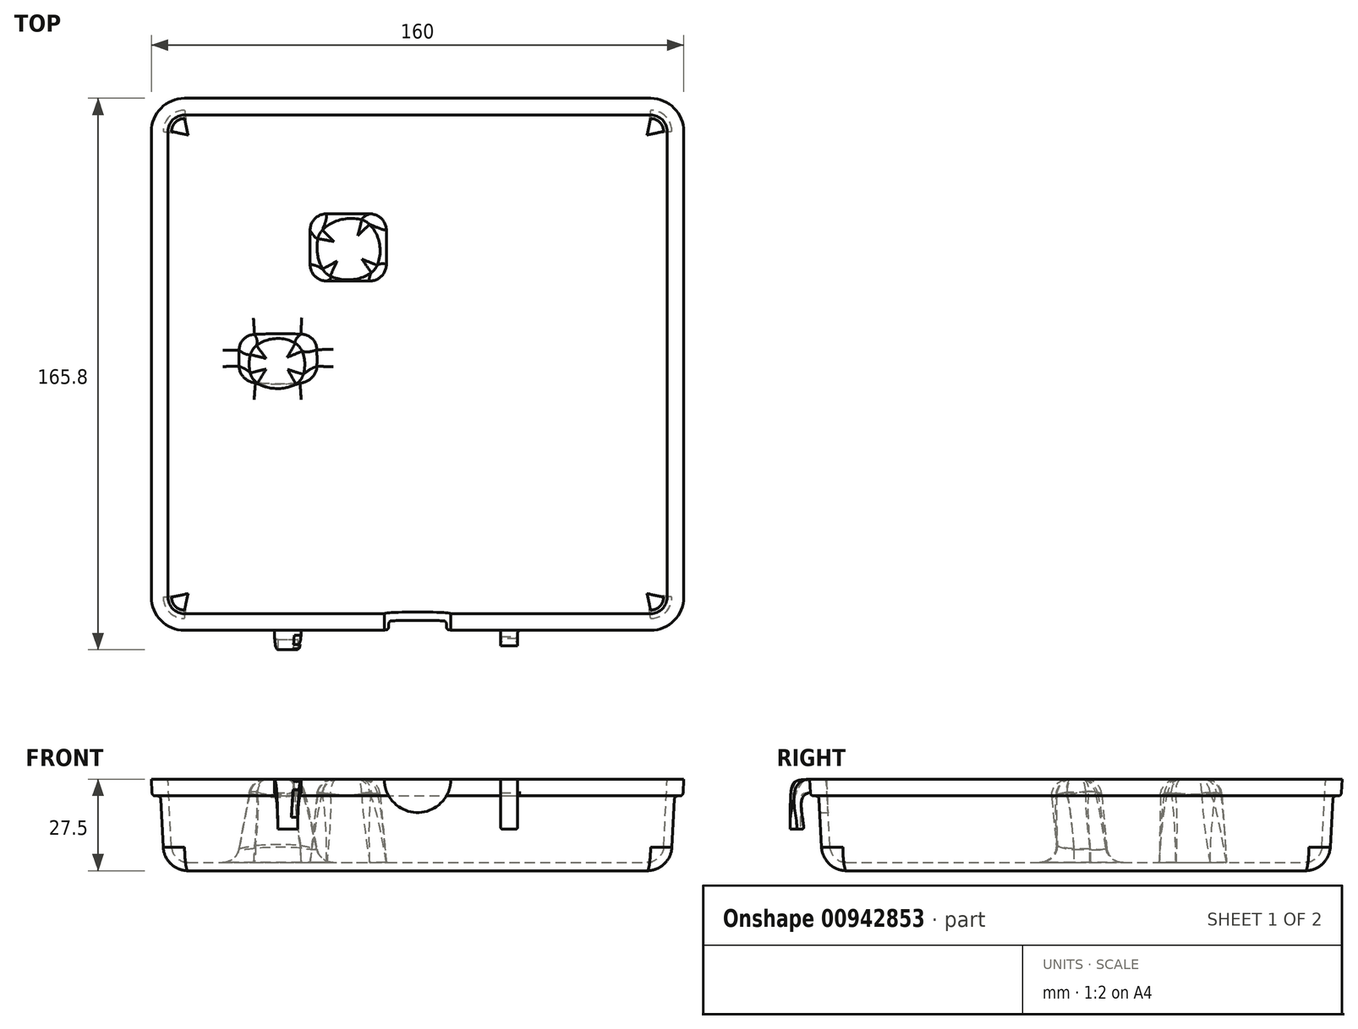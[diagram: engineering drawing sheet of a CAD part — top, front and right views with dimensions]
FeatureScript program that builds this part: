
annotation { "Feature Type Name" : "Feature", "Feature Type Description" : "" }
export const myFeature = defineFeature(function(context is Context, id is Id, definition is map)
    precondition{}
    {
        {
            var Q0;
            Q0=qCreatedBy(makeId("Top.planeOp"),FACE);
            var sketch = newSketch(context, id + "F0", { "sketchPlane" : qUnion([Q0])});
            skLineSegment(sketch, "E0.bottom", {"start": v(5, 0) * mm, "end": v(145, 0) * mm});
            skLineSegment(sketch, "E0.top", {"start": v(5, 150) * mm, "end": v(145, 150) * mm});
            skLineSegment(sketch, "E0.left", {"start": v(0, 5) * mm, "end": v(0, 145) * mm});
            skLineSegment(sketch, "E0.right", {"start": v(150, 5) * mm, "end": v(150, 145) * mm});
            skLineSegment(sketch, "E1.0", {"start": v(-5, 5) * mm, "end": v(-5, 145) * mm});
            skLineSegment(sketch, "E1.1", {"start": v(5, -5) * mm, "end": v(145, -5) * mm});
            skLineSegment(sketch, "E1.2", {"start": v(155, 5) * mm, "end": v(155, 145) * mm});
            skLineSegment(sketch, "E1.3", {"start": v(5, 155) * mm, "end": v(145, 155) * mm});
            skPoint(sketch, "E2.visualSharp", {"position": v(0, 150) * mm});
            skArc(sketch, "E2.filletArc", {"start": v(5, 150) * mm, "mid": v(1.46, 148.54) * mm, "end": v(0, 145) * mm});
            skPoint(sketch, "E3.visualSharp", {"position": v(150, 150) * mm});
            skArc(sketch, "E3.filletArc", {"start": v(150, 145) * mm, "mid": v(148.54, 148.54) * mm, "end": v(145, 150) * mm});
            skPoint(sketch, "E4.visualSharp", {"position": v(150, 0) * mm});
            skArc(sketch, "E4.filletArc", {"start": v(145, 0) * mm, "mid": v(148.54, 1.46) * mm, "end": v(150, 5) * mm});
            skPoint(sketch, "E5.visualSharp", {"position": v(0, 0) * mm});
            skArc(sketch, "E5.filletArc", {"start": v(0, 5) * mm, "mid": v(1.46, 1.46) * mm, "end": v(5, 0) * mm});
            skPoint(sketch, "E6.visualSharp", {"position": v(-5, 155) * mm});
            skArc(sketch, "E6.filletArc", {"start": v(5, 155) * mm, "mid": v(-2.07, 152.07) * mm, "end": v(-5, 145) * mm});
            skPoint(sketch, "E7.visualSharp", {"position": v(155, 155) * mm});
            skArc(sketch, "E7.filletArc", {"start": v(155, 145) * mm, "mid": v(152.07, 152.07) * mm, "end": v(145, 155) * mm});
            skPoint(sketch, "E8.visualSharp", {"position": v(155, -5) * mm});
            skArc(sketch, "E8.filletArc", {"start": v(145, -5) * mm, "mid": v(152.07, -2.07) * mm, "end": v(155, 5) * mm});
            skPoint(sketch, "E9.visualSharp", {"position": v(-5, -5) * mm});
            skArc(sketch, "E9.filletArc", {"start": v(-5, 5) * mm, "mid": v(-2.07, -2.07) * mm, "end": v(5, -5) * mm});
            skSolve(sketch);
        }
        {
            var Q0;
            Q0=makeQuery(id+"F0.imprint","IMPRINT",FACE,{"disambiguationData":[TD([[makeQuery(id+"F0.imprint","IMPRINT",EDGE,{"derivedFrom":sQuery(id+"F0.wireOp",EDGE,"E0.bottom")}),1.0]])]});
            extrude(context, id + "F1", {"entities" : qUnion([Q0]), "oppositeDirection" : true, "depth" : 25 * mm, "hasDraft" : true, "draftAngle" : 3 * degree, "draftPullDirection" : true});
        }
        {
            var Q0;
            Q0=makeQuery(id+"F1.opExtrude","SWEPT_EDGE",EDGE,{"disambiguationData":[OSD([sQuery(id+"F0.wireOp",EDGE,"E0.bottom"),sQuery(id+"F0.wireOp",EDGE,"E0.left")])]});
            var Q1;
            Q1=makeQuery(id+"F1.opExtrude","SWEPT_EDGE",EDGE,{"disambiguationData":[OSD([sQuery(id+"F0.wireOp",EDGE,"E0.bottom"),sQuery(id+"F0.wireOp",EDGE,"E0.right")])]});
            var Q2;
            Q2=makeQuery(id+"F1.opExtrude","SWEPT_EDGE",EDGE,{"disambiguationData":[OSD([sQuery(id+"F0.wireOp",EDGE,"E0.top"),sQuery(id+"F0.wireOp",EDGE,"E0.left")])]});
            var Q3;
            Q3=makeQuery(id+"F1.opExtrude","SWEPT_EDGE",EDGE,{"disambiguationData":[OSD([sQuery(id+"F0.wireOp",EDGE,"E0.top"),sQuery(id+"F0.wireOp",EDGE,"E0.right")])]});
            var Q4;
            Q4=makeQuery(id+"F1.opExtrude","CAP_FACE",FACE,{"disambiguationData":[OSD([sQuery(id+"F0.wireOp",EDGE,"E0.bottom"),sQuery(id+"F0.wireOp",EDGE,"E0.top"),sQuery(id+"F0.wireOp",EDGE,"E0.left"),sQuery(id+"F0.wireOp",EDGE,"E0.right")])],"isStart":false});
            fillet(context, id + "F2", {"entities" : qUnion([Q0, Q1, Q2, Q3, Q4]), "radius" : 5 * mm, "tangentPropagation" : true, "allowEdgeOverflow" : false});
        }
        {
            var Q0;
            Q0=makeQuery(id+"F1.opExtrude","CAP_FACE",FACE,{"disambiguationData":[OSD([sQuery(id+"F0.wireOp",EDGE,"E0.bottom"),sQuery(id+"F0.wireOp",EDGE,"E0.top"),sQuery(id+"F0.wireOp",EDGE,"E0.left"),sQuery(id+"F0.wireOp",EDGE,"E0.right")])],"isStart":true});
            shell(context, id + "F3", {"entities" : qUnion([Q0]), "thickness" : 2.5 * mm, "oppositeDirection" : true});
        }
        {
            var Q0;
            Q0=makeQuery(id+"F0.imprint","IMPRINT",FACE,{"disambiguationData":[TD([[makeQuery(id+"F0.imprint","IMPRINT",EDGE,{"derivedFrom":sQuery(id+"F0.wireOp",EDGE,"E0.bottom")}),-1.0]])]});
            extrude(context, id + "F4", {"entities" : qUnion([Q0]), "operationType" : NewBodyOperationType.ADD, "oppositeDirection" : true, "depth" : 5 * mm, "hasDraft" : true, "draftAngle" : 3 * degree, "draftPullDirection" : true});
        }
        {
            var Q0;
            {var subQ0=sQuery(id+"F0.wireOp",EDGE,"E0.bottom");Q0=makeQuery(id+"F4.boolean.opBoolean","INTERSECT",EDGE,{"derivedFrom":[makeQuery(id+"F1.opExtrude","SWEPT_FACE",FACE,{"disambiguationData":[OSD([subQ0])]}),makeQuery(id+"F4.opExtrude","CAP_FACE",FACE,{"disambiguationData":[OSD([subQ0,sQuery(id+"F0.wireOp",EDGE,"E0.top"),sQuery(id+"F0.wireOp",EDGE,"E0.left"),sQuery(id+"F0.wireOp",EDGE,"E0.right"),sQuery(id+"F0.wireOp",EDGE,"E1.0"),sQuery(id+"F0.wireOp",EDGE,"E1.1"),sQuery(id+"F0.wireOp",EDGE,"E1.2"),sQuery(id+"F0.wireOp",EDGE,"E1.3"),sQuery(id+"F0.wireOp",EDGE,"E2.filletArc"),sQuery(id+"F0.wireOp",EDGE,"E3.filletArc"),sQuery(id+"F0.wireOp",EDGE,"E4.filletArc"),sQuery(id+"F0.wireOp",EDGE,"E5.filletArc"),sQuery(id+"F0.wireOp",EDGE,"E6.filletArc"),sQuery(id+"F0.wireOp",EDGE,"E7.filletArc"),sQuery(id+"F0.wireOp",EDGE,"E8.filletArc"),sQuery(id+"F0.wireOp",EDGE,"E9.filletArc")])],"isStart":false})]});}
            var Q1;
            Q1=makeQuery(id+"F4.opExtrude","CAP_EDGE",EDGE,{"disambiguationData":[OSD([sQuery(id+"F0.wireOp",EDGE,"E1.1")])],"isStart":false});
            fillet(context, id + "F5", {"entities" : qUnion([Q0, Q1]), "radius" : 1 * mm, "tangentPropagation" : true, "allowEdgeOverflow" : false});
        }
        {
            var Q0;
            Q0=qCreatedBy(makeId("Front.planeOp"),FACE);
            var sketch = newSketch(context, id + "F6", { "sketchPlane" : qUnion([Q0])});
            skCircle(sketch, "E10", {"center": v(75, 0) * mm, "radius": 10 * mm});
            skSolve(sketch);
        }
        {
            var Q0;
            Q0=qSketchRegion(id+"F6",true);
            extrude(context, id + "F7", {"entities" : qUnion([Q0]), "operationType" : NewBodyOperationType.REMOVE, "endBound" : BoundingType.SYMMETRIC, "depth" : 25 * mm});
        }
        {
            var Q0;
            Q0=qCreatedBy(makeId("Top.planeOp"),FACE);
            cPlane(context, id + "F8", {"entities" : qUnion([Q0]), "cplaneType" : CPlaneType.OFFSET, "offset" : 15 * mm, "oppositeDirection" : true, "width" : 150 * mm, "height" : 150 * mm});
        }
        {
            var Q0;
            {var subQ0=sQuery(id+"F0.wireOp",EDGE,"E1.1");var subQ1=sQuery(id+"F0.wireOp",EDGE,"E8.filletArc");Q0=makeQuery(id+"F7.boolean.opBoolean","SPLIT",FACE,{"disambiguationData":[TD([makeQuery(id+"F4.opExtrude","SWEPT_FACE",FACE,{"disambiguationData":[OSD([subQ1])]})])],"derivedFrom":makeQuery(id+"F4.opExtrude","SWEPT_FACE",FACE,{"disambiguationData":[OSD([subQ0])]})});}
            var sketch = newSketch(context, id + "F9", { "sketchPlane" : qUnion([Q0])});
            skLineSegment(sketch, "E11.bottom", {"start": v(100, 0.26) * mm, "end": v(105, 0.26) * mm});
            skLineSegment(sketch, "E11.top", {"start": v(100, -3.8) * mm, "end": v(105, -3.8) * mm});
            skLineSegment(sketch, "E11.left", {"start": v(100, 0.26) * mm, "end": v(100, -3.8) * mm});
            skLineSegment(sketch, "E11.right", {"start": v(105, 0.26) * mm, "end": v(105, -3.8) * mm});
            skSolve(sketch);
        }
        {
            var Q0;
            Q0=qCreatedBy(id+"F8.planeOp",FACE);
            var sketch = newSketch(context, id + "F10", { "sketchPlane" : qUnion([Q0])});
            skLineSegment(sketch, "E12.bottom", {"start": v(100, -6.79) * mm, "end": v(105, -6.79) * mm});
            skLineSegment(sketch, "E12.top", {"start": v(100, -8.79) * mm, "end": v(105, -8.79) * mm});
            skLineSegment(sketch, "E12.left", {"start": v(100, -6.79) * mm, "end": v(100, -8.79) * mm});
            skLineSegment(sketch, "E12.right", {"start": v(105, -6.79) * mm, "end": v(105, -8.79) * mm});
            skSolve(sketch);
        }
        {
            var Q1;
            Q1=makeQuery(id+"F9.imprint","IMPRINT",FACE,{"disambiguationData":[TD([[makeQuery(id+"F9.imprint","IMPRINT",EDGE,{"derivedFrom":sQuery(id+"F9.wireOp",EDGE,"E11.bottom")}),-1.0]])]});
            var Q2;
            Q2=makeQuery(id+"F10.imprint","IMPRINT",FACE,{"disambiguationData":[TD([[makeQuery(id+"F10.imprint","IMPRINT",EDGE,{"derivedFrom":sQuery(id+"F10.wireOp",EDGE,"E12.bottom")}),-1.0]])]});
            loft(context, id + "F11", {"operationType" : NewBodyOperationType.ADD, "startCondition" : LoftEndDerivativeType.NORMAL_TO_PROFILE, "startMagnitude" : 4, "endCondition" : LoftEndDerivativeType.NORMAL_TO_PROFILE, "endMagnitude" : 1, "sheetProfilesArray" : [{ "sheetProfileEntities" : qUnion([Q1]) }, { "sheetProfileEntities" : qUnion([Q2]) }]});
        }
        {
            var Q0;
            Q0=makeQuery(id+"F11.opLoft","MID_CAP_EDGE",EDGE,{"disambiguationData":[OSD([sQuery(id+"F0.wireOp",EDGE,"E1.1"),sQuery(id+"F9.wireOp",EDGE,"E11.bottom"),sQuery(id+"F9.wireOp",EDGE,"E11.top"),sQuery(id+"F9.wireOp",EDGE,"E11.right")])],"capPos":0.0});
            fillet(context, id + "F12", {"entities" : qUnion([Q0]), "radius" : 1 * mm, "tangentPropagation" : true, "allowEdgeOverflow" : false});
        }
        {
            var Q0;
            Q0=makeQuery(id+"F11.opLoft","CAP_FACE",FACE,{"disambiguationData":[OSD([makeQuery(id+"F10.imprint","IMPRINT",FACE,{"disambiguationData":[TD([[makeQuery(id+"F10.imprint","IMPRINT",EDGE,{"derivedFrom":sQuery(id+"F10.wireOp",EDGE,"E12.bottom")}),-1.0]])]})])],"isStart":true});
            fillet(context, id + "F13", {"entities" : qUnion([Q0]), "radius" : .5 * mm, "tangentPropagation" : true, "allowEdgeOverflow" : false});
        }
        {
            var Q0;
            Q0=makeQuery(id+"F3.opShell","OFFSET_FACE",FACE,{"disambiguationData":[OSD([sQuery(id+"F0.wireOp",EDGE,"E0.bottom"),sQuery(id+"F0.wireOp",EDGE,"E0.top"),sQuery(id+"F0.wireOp",EDGE,"E0.left"),sQuery(id+"F0.wireOp",EDGE,"E0.right"),sQuery(id+"F0.wireOp",EDGE,"E2.filletArc"),sQuery(id+"F0.wireOp",EDGE,"E3.filletArc"),sQuery(id+"F0.wireOp",EDGE,"E4.filletArc"),sQuery(id+"F0.wireOp",EDGE,"E5.filletArc")])]});
            var sketch = newSketch(context, id + "F14", { "sketchPlane" : qUnion([Q0])});
            skLineSegment(sketch, "E13.bottom", {"start": v(42.7, 100.07) * mm, "end": v(65.63, 100.07) * mm});
            skLineSegment(sketch, "E13.top", {"start": v(42.7, 120.25) * mm, "end": v(65.63, 120.25) * mm});
            skLineSegment(sketch, "E13.left", {"start": v(42.7, 100.07) * mm, "end": v(42.7, 120.25) * mm});
            skLineSegment(sketch, "E13.right", {"start": v(65.63, 100.07) * mm, "end": v(65.63, 120.25) * mm});
            skSolve(sketch);
        }
        {
            var Q0;
            Q0=qCreatedBy(makeId("Top.planeOp"),FACE);
            var sketch = newSketch(context, id + "F15", { "sketchPlane" : qUnion([Q0])});
            skArc(sketch, "E14", {"start": v(48.26, 102.79) * mm, "mid": v(55.2, 100.54) * mm, "end": v(61.55, 104.16) * mm});
            skArc(sketch, "E15", {"start": v(58.35, 117.61) * mm, "mid": v(51.16, 118.02) * mm, "end": v(45.95, 113.06) * mm});
            skArc(sketch, "E16", {"start": v(45.95, 113.06) * mm, "mid": v(45.46, 107.55) * mm, "end": v(48.26, 102.79) * mm});
            skArc(sketch, "E17", {"start": v(61.55, 104.16) * mm, "mid": v(63.08, 111.63) * mm, "end": v(58.35, 117.61) * mm});
            skSolve(sketch);
        }
        {
            var Q1;
            Q1=makeQuery(id+"F14.imprint","IMPRINT",FACE,{"disambiguationData":[TD([[makeQuery(id+"F14.imprint","IMPRINT",EDGE,{"derivedFrom":sQuery(id+"F14.wireOp",EDGE,"E13.bottom")}),1.0]])]});
            var Q2;
            Q2=makeQuery(id+"F15.imprint","IMPRINT",FACE,{"disambiguationData":[TD([[makeQuery(id+"F15.imprint","IMPRINT",EDGE,{"derivedFrom":sQuery(id+"F15.wireOp",EDGE,"E14")}),1.0]])]});
            var Q3;
            Q3=sQuery(id+"F14.wireOp",VERTEX,"E13.right.start");
            var Q4;
            Q4=sQuery(id+"F15.wireOp",VERTEX,"E16.end");
            loft(context, id + "F16", {"operationType" : NewBodyOperationType.ADD, "sheetProfilesArray" : [{ "sheetProfileEntities" : qUnion([Q1]) }, { "sheetProfileEntities" : qUnion([Q2]) }], "connections" : [{ "connectionEntities" : qUnion([Q3, Q4]), "connectionEdgeQueries" : qUnion([]), "connectionEdgeParameters" : [] }]});
        }
        {
            var Q0;
            Q0=makeQuery(id+"F16.opLoft","SWEPT_EDGE",EDGE,{"disambiguationData":[OSD([sQuery(id+"F14.wireOp",EDGE,"E13.bottom"),sQuery(id+"F14.wireOp",EDGE,"E13.left"),sQuery(id+"F15.wireOp",EDGE,"E14"),sQuery(id+"F15.wireOp",EDGE,"E16")])]});
            var Q1;
            Q1=makeQuery(id+"F16.opLoft","SWEPT_EDGE",EDGE,{"disambiguationData":[OSD([sQuery(id+"F14.wireOp",EDGE,"E13.bottom"),sQuery(id+"F14.wireOp",EDGE,"E13.right"),sQuery(id+"F15.wireOp",EDGE,"E14"),sQuery(id+"F15.wireOp",EDGE,"E17")])]});
            var Q2;
            Q2=makeQuery(id+"F16.opLoft","SWEPT_EDGE",EDGE,{"disambiguationData":[OSD([sQuery(id+"F14.wireOp",EDGE,"E13.top"),sQuery(id+"F14.wireOp",EDGE,"E13.right"),sQuery(id+"F15.wireOp",EDGE,"E15"),sQuery(id+"F15.wireOp",EDGE,"E17")])]});
            var Q3;
            Q3=makeQuery(id+"F16.opLoft","SWEPT_EDGE",EDGE,{"disambiguationData":[OSD([sQuery(id+"F14.wireOp",EDGE,"E13.top"),sQuery(id+"F14.wireOp",EDGE,"E13.left"),sQuery(id+"F15.wireOp",EDGE,"E15"),sQuery(id+"F15.wireOp",EDGE,"E16")])]});
            fillet(context, id + "F17", {"entities" : qUnion([Q0, Q1, Q2, Q3]), "radius" : 5 * mm, "tangentPropagation" : true, "allowEdgeOverflow" : false});
        }
        {
            var Q0;
            Q0=makeQuery(id+"F16.opLoft","MID_CAP_EDGE",EDGE,{"disambiguationData":[OSD([sQuery(id+"F14.wireOp",EDGE,"E13.bottom"),sQuery(id+"F14.wireOp",EDGE,"E13.top"),sQuery(id+"F14.wireOp",EDGE,"E13.left")])],"capPos":0.0});
            var Q1;
            Q1=makeQuery(id+"F16.opLoft","MID_CAP_EDGE",EDGE,{"disambiguationData":[OSD([sQuery(id+"F15.wireOp",EDGE,"E14"),sQuery(id+"F15.wireOp",EDGE,"E15"),sQuery(id+"F15.wireOp",EDGE,"E16")])],"capPos":1.0});
            fillet(context, id + "F18", {"entities" : qUnion([Q0, Q1]), "radius" : 5 * mm, "tangentPropagation" : true, "allowEdgeOverflow" : false});
        }
        {
            var Q0;
            Q0=makeQuery(id+"F14.imprint","IMPRINT",FACE,{"disambiguationData":[TD([[makeQuery(id+"F14.imprint","IMPRINT",EDGE,{"derivedFrom":sQuery(id+"F14.wireOp",EDGE,"E13.bottom")}),-1.0]])]});
            var sketch = newSketch(context, id + "F19", { "sketchPlane" : qUnion([Q0])});
            skLineSegment(sketch, "E18.bottom", {"start": v(20.62, 69.63) * mm, "end": v(45.62, 69.63) * mm});
            skLineSegment(sketch, "E18.top", {"start": v(20.62, 84.63) * mm, "end": v(45.62, 84.63) * mm});
            skLineSegment(sketch, "E18.left", {"start": v(20.62, 69.63) * mm, "end": v(20.62, 84.63) * mm});
            skLineSegment(sketch, "E18.right", {"start": v(45.62, 69.63) * mm, "end": v(45.62, 84.63) * mm});
            skSolve(sketch);
        }
        {
            var Q0;
            Q0=qCreatedBy(makeId("Top.planeOp"),FACE);
            var sketch = newSketch(context, id + "F20", { "sketchPlane" : qUnion([Q0])});
            skArc(sketch, "E19", {"start": v(38.94, 70.46) * mm, "mid": v(40.28, 75.1) * mm, "end": v(38.54, 79.62) * mm});
            skArc(sketch, "E20", {"start": v(38.54, 79.62) * mm, "mid": v(32.07, 82.32) * mm, "end": v(26.16, 78.56) * mm});
            skArc(sketch, "E21", {"start": v(26.16, 78.56) * mm, "mid": v(25.14, 74.72) * mm, "end": v(26.21, 70.9) * mm});
            skArc(sketch, "E22", {"start": v(26.21, 70.9) * mm, "mid": v(32.46, 67.2) * mm, "end": v(38.94, 70.46) * mm});
            skLineSegment(sketch, "E23", {"start": v(26.16, 78.56) * mm, "end": v(32.72, 74.78) * mm, "construction": true});
            skLineSegment(sketch, "E24", {"start": v(38.54, 79.62) * mm, "end": v(32.72, 74.78) * mm, "construction": true});
            skLineSegment(sketch, "E25", {"start": v(38.94, 70.46) * mm, "end": v(32.72, 74.78) * mm, "construction": true});
            skLineSegment(sketch, "E26", {"start": v(32.72, 74.78) * mm, "end": v(26.21, 70.9) * mm, "construction": true});
            skLineSegment(sketch, "E27", {"start": v(32.72, 74.78) * mm, "end": v(18.64, 74.78) * mm, "construction": true});
            skSolve(sketch);
        }
        {
            var Q1;
            Q1=makeQuery(id+"F19.imprint","IMPRINT",FACE,{"disambiguationData":[TD([[makeQuery(id+"F19.imprint","IMPRINT",EDGE,{"derivedFrom":sQuery(id+"F19.wireOp",EDGE,"E18.bottom")}),1.0]])]});
            var Q2;
            Q2=makeQuery(id+"F20.imprint","IMPRINT",FACE,{"disambiguationData":[TD([[makeQuery(id+"F20.imprint","IMPRINT",EDGE,{"derivedFrom":sQuery(id+"F20.wireOp",EDGE,"E19")}),1.0]])]});
            loft(context, id + "F21", {"operationType" : NewBodyOperationType.ADD, "sheetProfilesArray" : [{ "sheetProfileEntities" : qUnion([Q1]) }, { "sheetProfileEntities" : qUnion([Q2]) }]});
        }
        {
            var Q0;
            Q0=makeQuery(id+"F21.opLoft","SWEPT_EDGE",EDGE,{"disambiguationData":[OSD([sQuery(id+"F19.wireOp",EDGE,"E18.bottom"),sQuery(id+"F19.wireOp",EDGE,"E18.left"),sQuery(id+"F20.wireOp",EDGE,"E21"),sQuery(id+"F20.wireOp",EDGE,"E22")])]});
            var Q1;
            Q1=makeQuery(id+"F21.opLoft","SWEPT_EDGE",EDGE,{"disambiguationData":[OSD([sQuery(id+"F19.wireOp",EDGE,"E18.bottom"),sQuery(id+"F19.wireOp",EDGE,"E18.right"),sQuery(id+"F20.wireOp",EDGE,"E19"),sQuery(id+"F20.wireOp",EDGE,"E22")])]});
            var Q2;
            Q2=makeQuery(id+"F21.opLoft","SWEPT_EDGE",EDGE,{"disambiguationData":[OSD([sQuery(id+"F19.wireOp",EDGE,"E18.top"),sQuery(id+"F19.wireOp",EDGE,"E18.right"),sQuery(id+"F20.wireOp",EDGE,"E19"),sQuery(id+"F20.wireOp",EDGE,"E20")])]});
            var Q3;
            Q3=makeQuery(id+"F21.opLoft","SWEPT_EDGE",EDGE,{"disambiguationData":[OSD([sQuery(id+"F19.wireOp",EDGE,"E18.top"),sQuery(id+"F19.wireOp",EDGE,"E18.left"),sQuery(id+"F20.wireOp",EDGE,"E20"),sQuery(id+"F20.wireOp",EDGE,"E21")])]});
            fillet(context, id + "F22", {"entities" : qUnion([Q0, Q1, Q2, Q3]), "radius" : 5 * mm, "tangentPropagation" : true, "allowEdgeOverflow" : false});
        }
        {
            var Q0;
            Q0=makeQuery(id+"F22.opFillet","BLEND_EDGE",EDGE,{"blendedFrom":[makeQuery(id+"F21.opLoft","SWEPT_EDGE",EDGE,{"disambiguationData":[OSD([sQuery(id+"F19.wireOp",EDGE,"E18.bottom"),sQuery(id+"F19.wireOp",EDGE,"E18.right"),sQuery(id+"F20.wireOp",EDGE,"E19"),sQuery(id+"F20.wireOp",EDGE,"E22")])]}),makeQuery(id+"F3.opShell","OFFSET_FACE",FACE,{"disambiguationData":[OSD([sQuery(id+"F0.wireOp",EDGE,"E0.bottom"),sQuery(id+"F0.wireOp",EDGE,"E0.top"),sQuery(id+"F0.wireOp",EDGE,"E0.left"),sQuery(id+"F0.wireOp",EDGE,"E0.right"),sQuery(id+"F0.wireOp",EDGE,"E2.filletArc"),sQuery(id+"F0.wireOp",EDGE,"E3.filletArc"),sQuery(id+"F0.wireOp",EDGE,"E4.filletArc"),sQuery(id+"F0.wireOp",EDGE,"E5.filletArc")])]})],"blendedInto":[makeQuery(id+"F3.opShell","OFFSET_FACE",FACE,{"disambiguationData":[OSD([sQuery(id+"F0.wireOp",EDGE,"E0.bottom"),sQuery(id+"F0.wireOp",EDGE,"E0.top"),sQuery(id+"F0.wireOp",EDGE,"E0.left"),sQuery(id+"F0.wireOp",EDGE,"E0.right"),sQuery(id+"F0.wireOp",EDGE,"E2.filletArc"),sQuery(id+"F0.wireOp",EDGE,"E3.filletArc"),sQuery(id+"F0.wireOp",EDGE,"E4.filletArc"),sQuery(id+"F0.wireOp",EDGE,"E5.filletArc")])]})]});
            var Q1;
            Q1=makeQuery(id+"F21.opLoft","MID_CAP_EDGE",EDGE,{"disambiguationData":[OSD([sQuery(id+"F20.wireOp",EDGE,"E19"),sQuery(id+"F20.wireOp",EDGE,"E21"),sQuery(id+"F20.wireOp",EDGE,"E22")])],"capPos":1.0});
            fillet(context, id + "F23", {"entities" : qUnion([Q0, Q1]), "radius" : 5 * mm, "tangentPropagation" : true, "allowEdgeOverflow" : false});
        }
        {
            var Q0;
            {var subQ0=sQuery(id+"F0.wireOp",EDGE,"E1.1");var subQ1=sQuery(id+"F0.wireOp",EDGE,"E9.filletArc");Q0=makeQuery(id+"F7.boolean.opBoolean","SPLIT",FACE,{"disambiguationData":[TD([makeQuery(id+"F4.opExtrude","SWEPT_FACE",FACE,{"disambiguationData":[OSD([subQ1])]})])],"derivedFrom":makeQuery(id+"F4.opExtrude","SWEPT_FACE",FACE,{"disambiguationData":[OSD([subQ0])]})});}
            var sketch = newSketch(context, id + "F24", { "sketchPlane" : qUnion([Q0])});
            skLineSegment(sketch, "E28.bottom", {"start": v(32, -3.8) * mm, "end": v(40, -3.8) * mm});
            skLineSegment(sketch, "E28.top", {"start": v(32, 0.26) * mm, "end": v(40, 0.26) * mm});
            skLineSegment(sketch, "E28.left", {"start": v(32, -3.8) * mm, "end": v(32, 0.26) * mm});
            skLineSegment(sketch, "E28.right", {"start": v(40, -3.8) * mm, "end": v(40, 0.26) * mm});
            skLineSegment(sketch, "E29.bottom", {"start": v(38, 0.76) * mm, "end": v(42, 0.76) * mm});
            skLineSegment(sketch, "E29.top", {"start": v(38, 2.76) * mm, "end": v(42, 2.76) * mm});
            skLineSegment(sketch, "E29.left", {"start": v(38, 0.76) * mm, "end": v(38, 2.76) * mm});
            skLineSegment(sketch, "E29.right", {"start": v(42, 0.76) * mm, "end": v(42, 2.76) * mm});
            skSolve(sketch);
        }
        {
            var Q0;
            Q0=qCreatedBy(id+"F8.planeOp",FACE);
            var sketch = newSketch(context, id + "F25", { "sketchPlane" : qUnion([Q0])});
            skLineSegment(sketch, "E30.bottom", {"start": v(33, -7.79) * mm, "end": v(39, -7.79) * mm});
            skLineSegment(sketch, "E30.top", {"start": v(33, -10.79) * mm, "end": v(39, -10.79) * mm});
            skLineSegment(sketch, "E30.left", {"start": v(33, -7.79) * mm, "end": v(33, -10.79) * mm});
            skLineSegment(sketch, "E30.right", {"start": v(39, -7.79) * mm, "end": v(39, -10.79) * mm});
            skLineSegment(sketch, "E31.bottom", {"start": v(37, -11.04) * mm, "end": v(42.04, -11.04) * mm});
            skLineSegment(sketch, "E31.top", {"start": v(37, -13.04) * mm, "end": v(42.04, -13.04) * mm});
            skLineSegment(sketch, "E31.left", {"start": v(37, -11.04) * mm, "end": v(37, -13.04) * mm});
            skLineSegment(sketch, "E31.right", {"start": v(42.04, -11.04) * mm, "end": v(42.04, -13.04) * mm});
            skSolve(sketch);
        }
        {
            var Q1;
            {var subQ0=sQuery(id+"F24.wireOp",EDGE,"E28.left");Q1=makeQuery(id+"F24.imprint","IMPRINT",FACE,{"disambiguationData":[TD([[makeQuery(id+"F24.imprint","IMPRINT",EDGE,{"derivedFrom":subQ0}),-1.0]])]});}
            var Q2;
            Q2=makeQuery(id+"F25.imprint","IMPRINT",FACE,{"disambiguationData":[TD([[makeQuery(id+"F25.imprint","IMPRINT",EDGE,{"derivedFrom":sQuery(id+"F25.wireOp",EDGE,"E30.bottom")}),-1.0]])]});
            loft(context, id + "F26", {"operationType" : NewBodyOperationType.ADD, "startCondition" : LoftEndDerivativeType.NORMAL_TO_PROFILE, "startMagnitude" : 2.5, "endCondition" : LoftEndDerivativeType.NORMAL_TO_PROFILE, "endMagnitude" : 3, "sheetProfilesArray" : [{ "sheetProfileEntities" : qUnion([Q1]) }, { "sheetProfileEntities" : qUnion([Q2]) }]});
        }
        {
            var Q1;
            Q1=makeQuery(id+"F24.imprint","IMPRINT",FACE,{"disambiguationData":[TD([[makeQuery(id+"F24.imprint","IMPRINT",EDGE,{"derivedFrom":sQuery(id+"F24.wireOp",EDGE,"E29.bottom")}),1.0]])]});
            var Q2;
            Q2=makeQuery(id+"F25.imprint","IMPRINT",FACE,{"disambiguationData":[TD([[makeQuery(id+"F25.imprint","IMPRINT",EDGE,{"derivedFrom":sQuery(id+"F25.wireOp",EDGE,"E31.bottom")}),-1.0]])]});
            loft(context, id + "F27", {"operationType" : NewBodyOperationType.REMOVE, "startCondition" : LoftEndDerivativeType.NORMAL_TO_PROFILE, "startMagnitude" : 1.5, "endCondition" : LoftEndDerivativeType.NORMAL_TO_PROFILE, "endMagnitude" : 1, "sheetProfilesArray" : [{ "sheetProfileEntities" : qUnion([Q1]) }, { "sheetProfileEntities" : qUnion([Q2]) }]});
        }
    });
